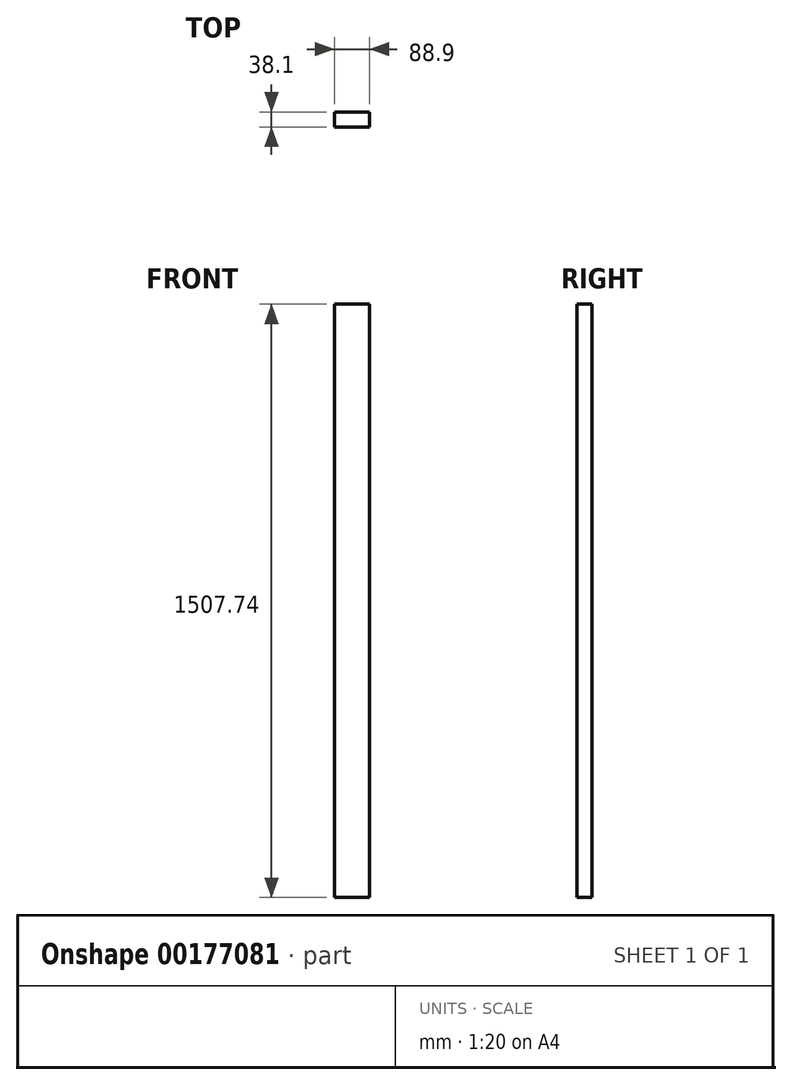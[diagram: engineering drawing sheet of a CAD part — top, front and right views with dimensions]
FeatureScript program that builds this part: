
annotation { "Feature Type Name" : "Feature", "Feature Type Description" : "" }
export const myFeature = defineFeature(function(context is Context, id is Id, definition is map)
    precondition{}
    {
        {
            var Q0;
            Q0=qCreatedBy(makeId("Top.planeOp"),FACE);
            var sketch = newSketch(context, id + "F0", { "sketchPlane" : qUnion([Q0])});
            skLineSegment(sketch, "E0.bottom", {"start": v(-80, 0) * mm, "end": v(-168.9, 0) * mm});
            skLineSegment(sketch, "E0.top", {"start": v(-80, 38.1) * mm, "end": v(-168.9, 38.1) * mm});
            skLineSegment(sketch, "E0.left", {"start": v(-80, 0) * mm, "end": v(-80, 38.1) * mm});
            skLineSegment(sketch, "E0.right", {"start": v(-168.9, 0) * mm, "end": v(-168.9, 38.1) * mm});
            skSolve(sketch);
        }
        {
            var Q0;
            Q0 = qSketchRegion(id + "F0", true);
            extrude(context, id + "F1", {"entities" : qUnion([Q0]), "depth" : 1507.74 * mm});
        }
    });
